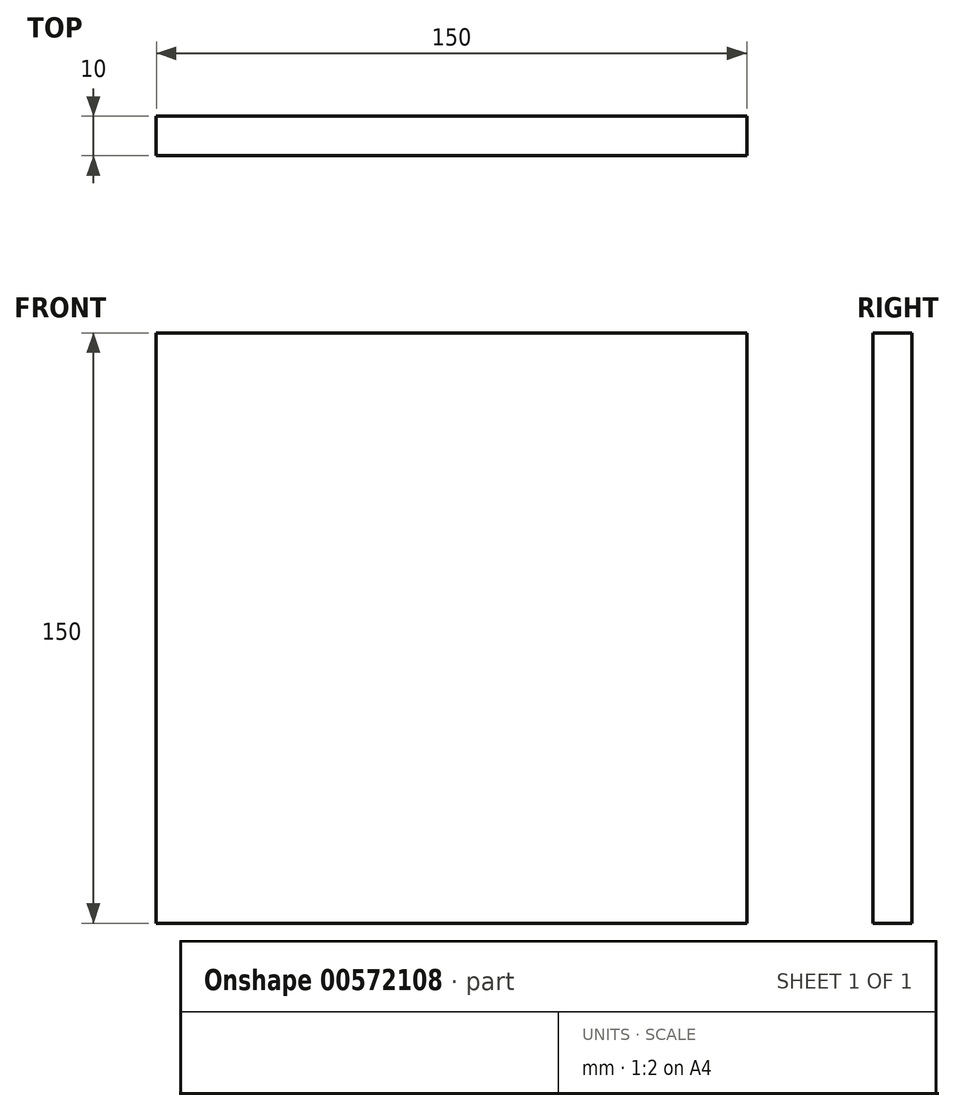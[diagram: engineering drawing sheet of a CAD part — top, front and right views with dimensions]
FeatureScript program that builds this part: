
annotation { "Feature Type Name" : "Feature", "Feature Type Description" : "" }
export const myFeature = defineFeature(function(context is Context, id is Id, definition is map)
    precondition{}
    {
        {
            var Q0;
            Q0=qCreatedBy(makeId("Front.planeOp"),FACE);
            var sketch = newSketch(context, id + "F0", { "sketchPlane" : qUnion([Q0])});
            skLineSegment(sketch, "E0.bottom", {"start": v(-75, 75) * mm, "end": v(75, 75) * mm});
            skLineSegment(sketch, "E0.top", {"start": v(-75, -75) * mm, "end": v(75, -75) * mm});
            skLineSegment(sketch, "E0.left", {"start": v(-75, 75) * mm, "end": v(-75, -75) * mm});
            skLineSegment(sketch, "E0.right", {"start": v(75, 75) * mm, "end": v(75, -75) * mm});
            skSolve(sketch);
        }
        {
            var Q0;
            Q0=makeQuery(id+"F0.imprint","IMPRINT",FACE,{"disambiguationData":[TD([[makeQuery(id+"F0.imprint","IMPRINT",EDGE,{"derivedFrom":sQuery(id+"F0.wireOp",EDGE,"E0.bottom")}),-1.0]])]});
            extrude(context, id + "F1", {"entities" : qUnion([Q0]), "depth" : 10 * mm, "offsetDistance" : 25 * mm});
        }
    });
